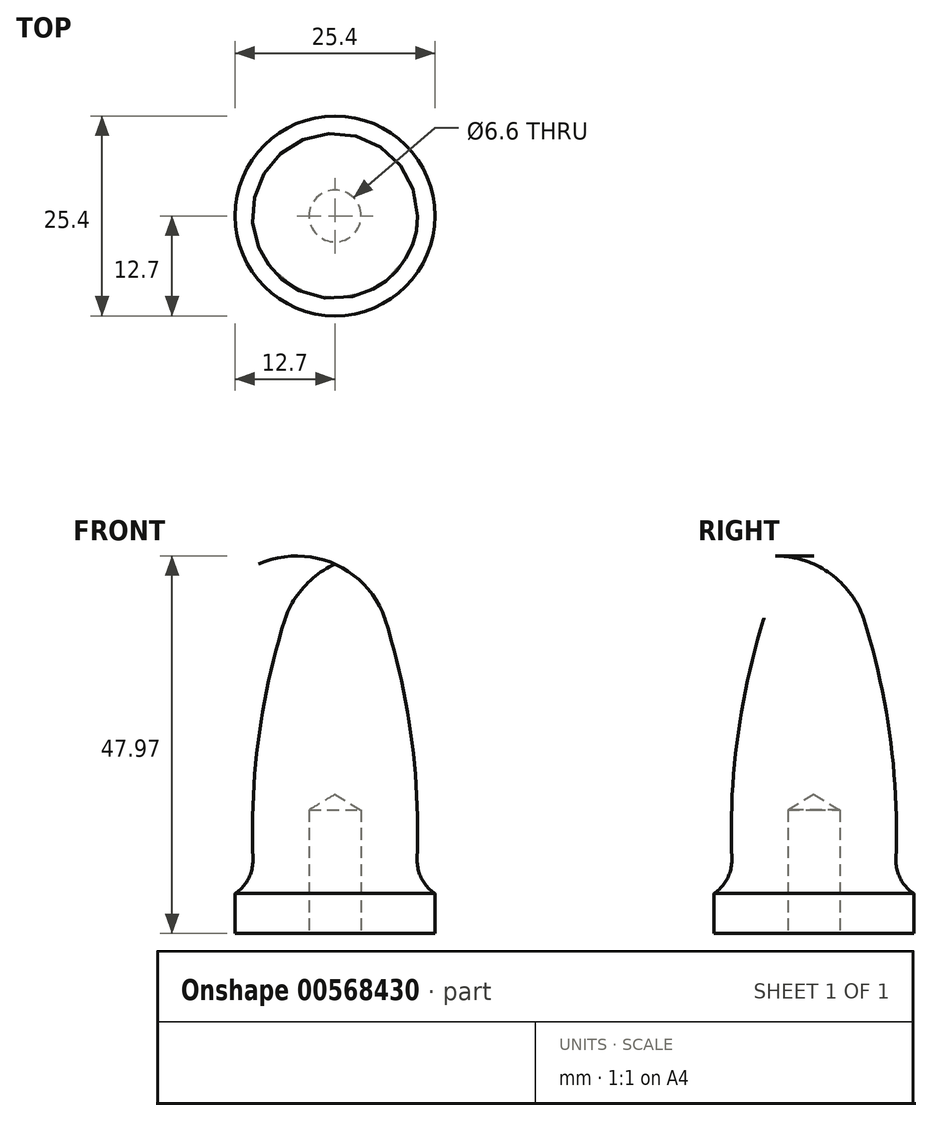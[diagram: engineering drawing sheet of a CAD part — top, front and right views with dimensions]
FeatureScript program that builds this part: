
annotation { "Feature Type Name" : "Feature", "Feature Type Description" : "" }
export const myFeature = defineFeature(function(context is Context, id is Id, definition is map)
    precondition{}
    {
        {
            var Q0;
            Q0=qCreatedBy(makeId("Front.planeOp"),FACE);
            var sketch = newSketch(context, id + "F0", { "sketchPlane" : qUnion([Q0])});
            skLineSegment(sketch, "E0", {"start": v(0, 0) * mm, "end": v(12.7, 0) * mm});
            skLineSegment(sketch, "E1", {"start": v(12.7, 0) * mm, "end": v(12.7, 5.08) * mm});
            skLineSegment(sketch, "E2", {"start": v(12.7, 5.08) * mm, "end": v(10.16, 5.08) * mm});
            skArc(sketch, "E3", {"start": v(10.16, 5.08) * mm, "mid": v(9.96, 22.71) * mm, "end": v(6.35, 39.98) * mm});
            skPoint(sketch, "E3.endSnap0", {"position": v(6.35, 0) * mm});
            skLineSegment(sketch, "E4", {"start": v(0, 0) * mm, "end": v(0, 39.98) * mm});
            skArc(sketch, "E5", {"start": v(6.35, 39.98) * mm, "mid": v(3.9, 44.11) * mm, "end": v(0, 46.93) * mm});
            skLineSegment(sketch, "E6", {"start": v(0, 46.93) * mm, "end": v(0, 39.98) * mm});
            skSolve(sketch);
        }
        {
            var Q0;
            Q0=makeQuery(id+"F0.imprint","IMPRINT",FACE,{"disambiguationData":[TD([[makeQuery(id+"F0.imprint","IMPRINT",EDGE,{"derivedFrom":sQuery(id+"F0.wireOp",EDGE,"E0")}),1.0]])]});
            var Q1;
            Q1=sQuery(id+"F0.wireOp",EDGE,"E4");
            revolve(context, id + "F1", {"entities" : qUnion([Q0]), "axis" : qUnion([Q1]), "revolveType" : RevolveType.FULL});
        }
        {
            var Q0;
            Q0=makeQuery(id+"F1.opRevolve","SWEPT_FACE",FACE,{"disambiguationData":[OSD([sQuery(id+"F0.wireOp",EDGE,"E5")])]});
            fillet(context, id + "F2", {"entities" : qUnion([Q0]), "radius" : 5.08 * mm, "tangentPropagation" : true, "allowEdgeOverflow" : false});
        }
        {
            var Q0;
            Q0=makeQuery(id+"F1.opRevolve","SWEPT_EDGE",EDGE,{"disambiguationData":[OSD([sQuery(id+"F0.wireOp",EDGE,"E2"),sQuery(id+"F0.wireOp",EDGE,"E3")])]});
            fillet(context, id + "F3", {"entities" : qUnion([Q0]), "radius" : 5.08 * mm, "tangentPropagation" : true, "allowEdgeOverflow" : false});
        }
        {
            var Q0;
            Q0=makeQuery(id+"F1.opRevolve","SWEPT_FACE",FACE,{"disambiguationData":[OSD([sQuery(id+"F0.wireOp",EDGE,"E0")])]});
            var sketch = newSketch(context, id + "F4", { "sketchPlane" : qUnion([Q0])});
            skCircle(sketch, "E7", {"center": v(0, 0) * mm, "radius": 6.35 * mm});
            skSolve(sketch);
        }
        {
            var Q0;
            Q0=sQuery(id+"F4.wireOp",VERTEX,"E7.center");
            var Q1;
            Q1=makeQuery(id+"F1.opRevolve","SWEPT_BODY",BODY,{"disambiguationData":[OSD([sQuery(id+"F0.wireOp",EDGE,"E0"),sQuery(id+"F0.wireOp",EDGE,"E1"),sQuery(id+"F0.wireOp",EDGE,"E2"),sQuery(id+"F0.wireOp",EDGE,"E3"),sQuery(id+"F0.wireOp",EDGE,"E4"),sQuery(id+"F0.wireOp",EDGE,"E5"),sQuery(id+"F0.wireOp",EDGE,"E6")])]});
            hole(context, id + "F5", {"style" : HoleStyle.SIMPLE, "endStyle" : HoleEndStyle.BLIND, "standardTappedOrClearance" : lookupTablePath({ "standard" : "ISO", "fit" : "Normal", "size" : "M6", "type" : "Clearance" }), "standardBlindInLast" : lookupTablePath({ "fit" : "Standard", "standard" : "ISO", "size" : "M6", "type" : "Clearance" }), "holeDiameter" : 6.6 * mm, "holeDepth" : 15.7 * mm, "isTappedThrough" : true, "tappedDepth" : 12.7 * mm, "tapClearance" : 3, "locations" : qUnion([Q0]), "scope" : qUnion([Q1])});
        }
    });
